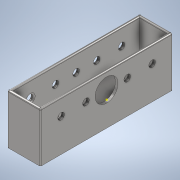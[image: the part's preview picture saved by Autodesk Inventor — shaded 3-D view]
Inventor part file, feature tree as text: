
AUTODESK INVENTOR PART (.ipt)
format: ipt  version: 2022 (Build 260153070, 153G)  size: 221,696 bytes
history: native  units: mm
features: sketch x13, extrude x6, fillet x1
ambient origin geometry x8: Origin, YZ Plane, XZ Plane, XY Plane, X Axis, Y Axis, Z Axis, Center Point
bodies: Solid1 (feature_tree)
feature tree (20):
  extrude  "Extrusion1"  Depth=203.2mm
  extrude  "Extrusion2"  Depth=4.0mm
  extrude  "Extrusion5"  Depth=4.0mm TaperAngle=0.0deg
  sketch  "Sketch6"  dims[d33=4.0mm d34=4.0mm d35=4.0mm]
  sketch  "Sketch7"  dims[d36=4.0mm d37=25.4mm]
  sketch  "Sketch8"  dims[d38=25.4mm d39=50.8mm]
  sketch  "Sketch9"  dims[d40=50.8mm]
  sketch  "Sketch10"  dims[d41=25.4mm]
  extrude  "Extrusion6"  Depth=4.0mm
  fillet  "Fillet1"  Radius=4.0mm
  sketch  "Sketch11"  dims[d42=25.4mm]
  sketch  "Sketch12"  dims[d43=25.4mm]
  extrude  "Extrusion7"  Depth=25.4mm
  extrude  "Extrusion8"  Depth=50.8mm
  sketch  "Sketch15"  dims[d47=10.0mm d48=10.0mm d49=10.0mm d50=10.0mm d51=31.75mm d52=69.85mm d53=31.75mm d54=69.85mm d55=25.4mm d56=25.4mm d57=25.4mm d58=25.4mm d59=0.0mm d60=0.0mm d61=2.0mm d62=10.0mm d63=50.8mm d64=4.0mm d65=0.0mm d66=35.0mm d67=4.0mm d68=0.0mm d69=23.4mm d17=0.5mm d18=0.872665mm d19=0.5mm d20=0.872665mm]
  sketch  "Sketch1"  dims[d0=76.2mm d1=203.2mm]
  sketch  "Sketch2"  dims[d2=50.8mm d3=0.0mm d4=4.0mm]
  sketch  "Sketch5"  dims[d5=4.0mm d6=47.8mm d7=0.0mm]
  sketch  "Sketch13"  dims[d44=25.4mm]
  sketch  "Sketch14"  dims[d45=0.0mm d46=0.0mm]
